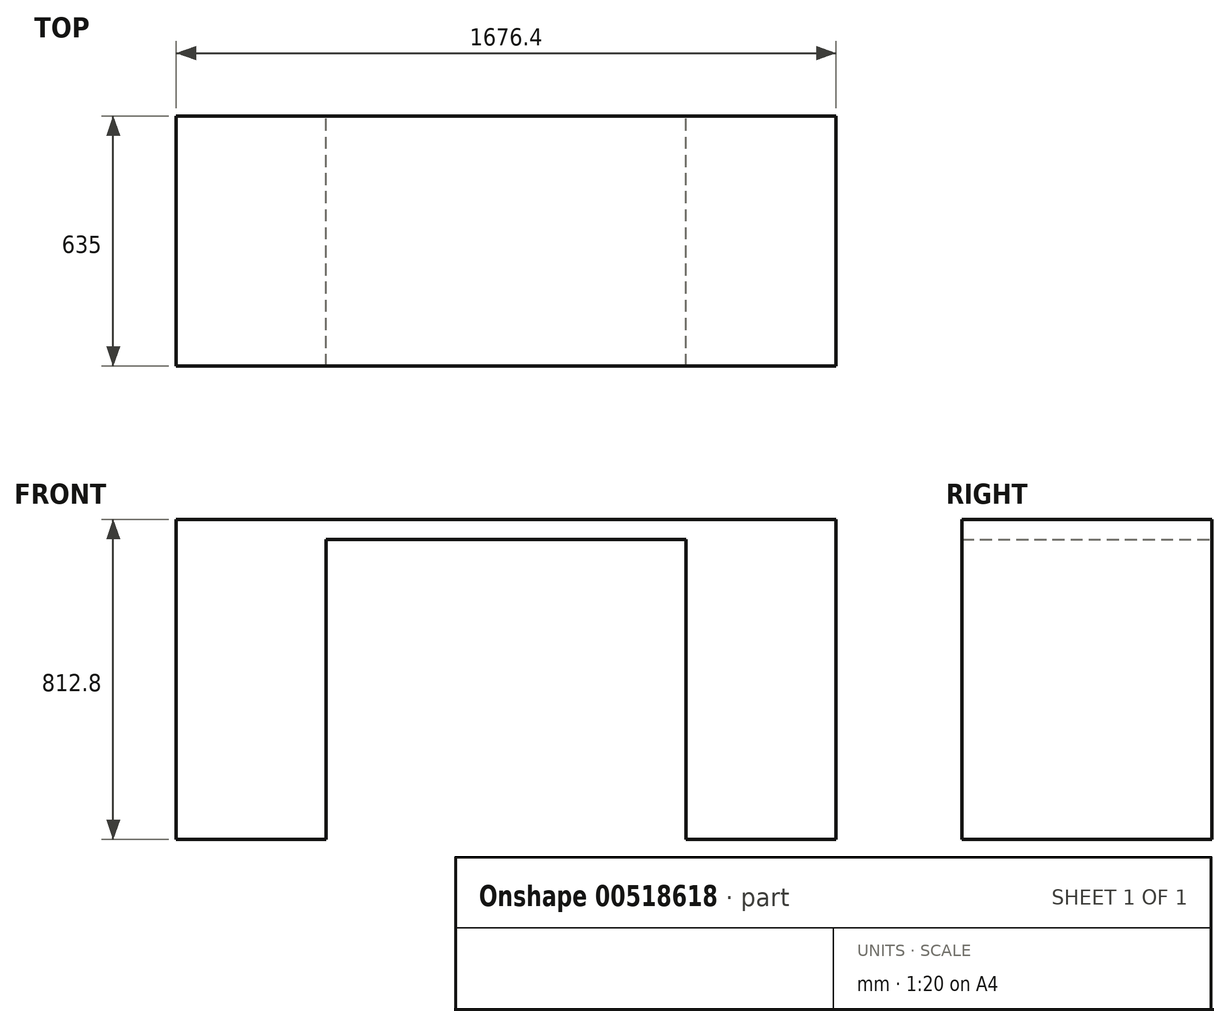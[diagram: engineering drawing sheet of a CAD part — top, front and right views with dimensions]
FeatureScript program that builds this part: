
annotation { "Feature Type Name" : "Feature", "Feature Type Description" : "" }
export const myFeature = defineFeature(function(context is Context, id is Id, definition is map)
    precondition{}
    {
        {
            var Q0;
            Q0=qCreatedBy(makeId("Front.planeOp"),FACE);
            var sketch = newSketch(context, id + "F0", { "sketchPlane" : qUnion([Q0])});
            skLineSegment(sketch, "E0.bottom", {"start": v(-838.2, -25.4) * mm, "end": v(838.2, -25.4) * mm});
            skLineSegment(sketch, "E0.top", {"start": v(-838.2, 25.4) * mm, "end": v(838.2, 25.4) * mm});
            skLineSegment(sketch, "E0.left", {"start": v(-838.2, -25.4) * mm, "end": v(-838.2, 25.4) * mm});
            skLineSegment(sketch, "E0.right", {"start": v(838.2, -25.4) * mm, "end": v(838.2, 25.4) * mm});
            skPoint(sketch, "E0.middle", {"position": v(0, 0) * mm});
            skLineSegment(sketch, "E1.bottom", {"start": v(-838.2, -25.4) * mm, "end": v(-457.2, -25.4) * mm});
            skLineSegment(sketch, "E1.top", {"start": v(-838.2, -787.4) * mm, "end": v(-457.2, -787.4) * mm});
            skLineSegment(sketch, "E1.left", {"start": v(-838.2, -25.4) * mm, "end": v(-838.2, -787.4) * mm});
            skLineSegment(sketch, "E1.right", {"start": v(-457.2, -25.4) * mm, "end": v(-457.2, -787.4) * mm});
            skLineSegment(sketch, "E2.bottom", {"start": v(838.2, -25.4) * mm, "end": v(457.2, -25.4) * mm});
            skLineSegment(sketch, "E2.top", {"start": v(838.2, -787.4) * mm, "end": v(457.2, -787.4) * mm});
            skLineSegment(sketch, "E2.left", {"start": v(838.2, -25.4) * mm, "end": v(838.2, -787.4) * mm});
            skLineSegment(sketch, "E2.right", {"start": v(457.2, -25.4) * mm, "end": v(457.2, -787.4) * mm});
            skLineSegment(sketch, "E3", {"start": v(-838.2, -431.8) * mm, "end": v(-457.2, -431.8) * mm});
            skLineSegment(sketch, "E4", {"start": v(-838.2, -215.9) * mm, "end": v(-457.2, -215.9) * mm});
            skLineSegment(sketch, "E5", {"start": v(457.2, -177.8) * mm, "end": v(838.2, -177.8) * mm});
            skLineSegment(sketch, "E6", {"start": v(457.2, -482.6) * mm, "end": v(838.2, -482.6) * mm});
            skSolve(sketch);
        }
        {
            var Q0;
            Q0=makeQuery(id+"F0.imprint","IMPRINT",FACE,{"disambiguationData":[TD([[makeQuery(id+"F0.imprint","IMPRINT",EDGE,{"derivedFrom":sQuery(id+"F0.wireOp",EDGE,"E0.bottom")}),1.0]])]});
            extrude(context, id + "F1", {"entities" : qUnion([Q0]), "depth" : 635 * mm, "offsetDistance" : 25.4 * mm});
        }
        {
            var Q0;
            Q0 = qSketchRegion(id + "F0", true);
            extrude(context, id + "F2", {"entities" : qUnion([Q0]), "operationType" : NewBodyOperationType.ADD, "depth" : 635 * mm, "offsetDistance" : 25.4 * mm});
        }
    });
